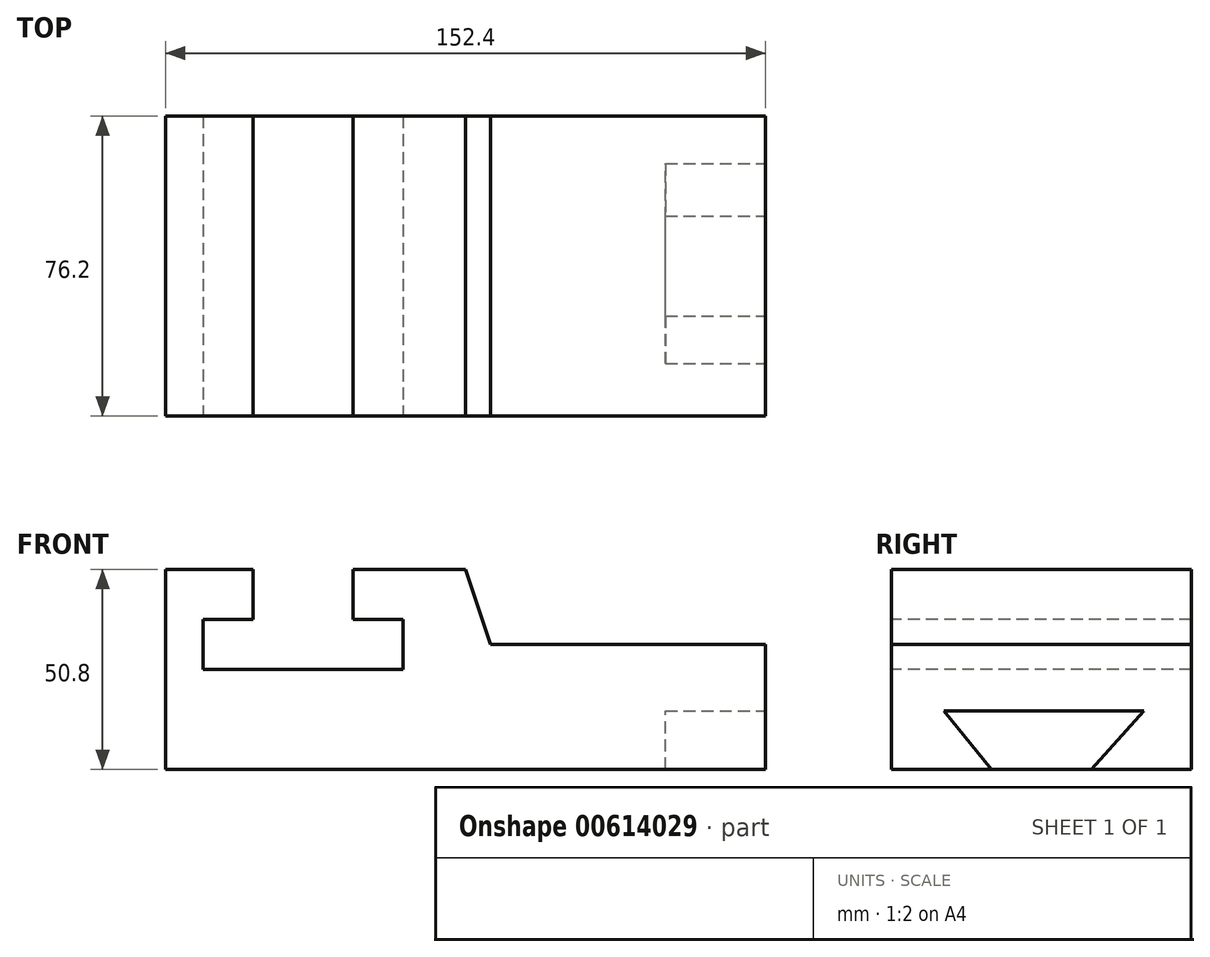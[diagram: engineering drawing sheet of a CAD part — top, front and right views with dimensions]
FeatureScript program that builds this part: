
annotation { "Feature Type Name" : "Feature", "Feature Type Description" : "" }
export const myFeature = defineFeature(function(context is Context, id is Id, definition is map)
    precondition{}
    {
        {
            var Q0;
            Q0=qCreatedBy(makeId("Front.planeOp"),FACE);
            var sketch = newSketch(context, id + "F0", { "sketchPlane" : qUnion([Q0])});
            skLineSegment(sketch, "E0", {"start": v(35.29, 0) * mm, "end": v(187.69, 0) * mm});
            skLineSegment(sketch, "E1", {"start": v(187.69, 0) * mm, "end": v(187.69, 31.75) * mm});
            skLineSegment(sketch, "E2", {"start": v(117.84, 31.75) * mm, "end": v(111.49, 50.8) * mm});
            skLineSegment(sketch, "E3", {"start": v(35.29, 0) * mm, "end": v(35.29, 50.8) * mm});
            skLineSegment(sketch, "E4", {"start": v(35.29, 50.8) * mm, "end": v(111.49, 50.8) * mm});
            skLineSegment(sketch, "E5", {"start": v(117.84, 31.75) * mm, "end": v(187.69, 31.75) * mm});
            skSolve(sketch);
        }
        {
            var Q0;
            Q0=makeQuery(id+"F0.imprint","IMPRINT",FACE,{"disambiguationData":[TD([[makeQuery(id+"F0.imprint","IMPRINT",EDGE,{"derivedFrom":sQuery(id+"F0.wireOp",EDGE,"E0")}),1.0]])]});
            extrude(context, id + "F1", {"entities" : qUnion([Q0]), "depth" : 76.2 * mm, "offsetDistance" : 25.4 * mm});
        }
        {
            var Q0;
            Q0=makeQuery(id+"F1.opExtrude","CAP_FACE",FACE,{"disambiguationData":[OSD([sQuery(id+"F0.wireOp",EDGE,"E0"),sQuery(id+"F0.wireOp",EDGE,"E1"),sQuery(id+"F0.wireOp",EDGE,"E2"),sQuery(id+"F0.wireOp",EDGE,"E3"),sQuery(id+"F0.wireOp",EDGE,"E4"),sQuery(id+"F0.wireOp",EDGE,"E5")])],"isStart":false});
            var sketch = newSketch(context, id + "F2", { "sketchPlane" : qUnion([Q0])});
            skLineSegment(sketch, "E6", {"start": v(35.29, 50.8) * mm, "end": v(35.29, 0) * mm});
            skLineSegment(sketch, "E7", {"start": v(35.29, 50.8) * mm, "end": v(57.5, 50.8) * mm});
            skLineSegment(sketch, "E8", {"start": v(57.5, 50.8) * mm, "end": v(57.5, 38.1) * mm});
            skLineSegment(sketch, "E9", {"start": v(57.5, 38.1) * mm, "end": v(44.8, 38.1) * mm});
            skLineSegment(sketch, "E10", {"start": v(44.8, 38.1) * mm, "end": v(44.8, 25.4) * mm});
            skLineSegment(sketch, "E11", {"start": v(44.8, 25.4) * mm, "end": v(95.6, 25.4) * mm});
            skLineSegment(sketch, "E12", {"start": v(95.6, 25.4) * mm, "end": v(95.6, 38.1) * mm});
            skLineSegment(sketch, "E13", {"start": v(95.6, 38.1) * mm, "end": v(82.9, 38.1) * mm});
            skLineSegment(sketch, "E14", {"start": v(82.9, 38.1) * mm, "end": v(82.9, 50.8) * mm});
            skSolve(sketch);
        }
        {
            var Q0;
            {var subQ0=sQuery(id+"F2.wireOp",EDGE,"E8");Q0=makeQuery(id+"F2.imprint","IMPRINT",FACE,{"disambiguationData":[TD([[makeQuery(id+"F2.imprint","IMPRINT",EDGE,{"derivedFrom":subQ0}),1.0]])]});}
            extrude(context, id + "F3", {"entities" : qUnion([Q0]), "operationType" : NewBodyOperationType.REMOVE, "oppositeDirection" : true, "depth" : 76.2 * mm, "offsetDistance" : 25.4 * mm});
        }
        {
            var Q0;
            Q0=makeQuery(id+"F1.opExtrude","SWEPT_FACE",FACE,{"disambiguationData":[OSD([sQuery(id+"F0.wireOp",EDGE,"E1")])]});
            var sketch = newSketch(context, id + "F4", { "sketchPlane" : qUnion([Q0])});
            skLineSegment(sketch, "E15", {"start": v(-76.2, 0) * mm, "end": v(-50.8, 0) * mm});
            skLineSegment(sketch, "E16", {"start": v(0, 0) * mm, "end": v(-25.4, 0) * mm});
            skLineSegment(sketch, "E17", {"start": v(-62.93, 14.86) * mm, "end": v(-12.13, 14.86) * mm});
            skLineSegment(sketch, "E18", {"start": v(-50.8, 0) * mm, "end": v(-25.4, 0) * mm});
            skPoint(sketch, "E19.endSnap0", {"position": v(-12.7, 0) * mm});
            skLineSegment(sketch, "E20", {"start": v(-50.8, 0) * mm, "end": v(-62.93, 14.86) * mm});
            skLineSegment(sketch, "E21", {"start": v(-12.13, 14.86) * mm, "end": v(-25.4, 0) * mm});
            skSolve(sketch);
        }
        {
            var Q0;
            Q0=makeQuery(id+"F4.imprint","IMPRINT",FACE,{"disambiguationData":[TD([[makeQuery(id+"F4.imprint","IMPRINT",EDGE,{"derivedFrom":sQuery(id+"F4.wireOp",EDGE,"E17")}),-1.0]])]});
            extrude(context, id + "F5", {"entities" : qUnion([Q0]), "operationType" : NewBodyOperationType.REMOVE, "oppositeDirection" : true, "depth" : 25.4 * mm, "offsetDistance" : 25.4 * mm});
        }
    });
